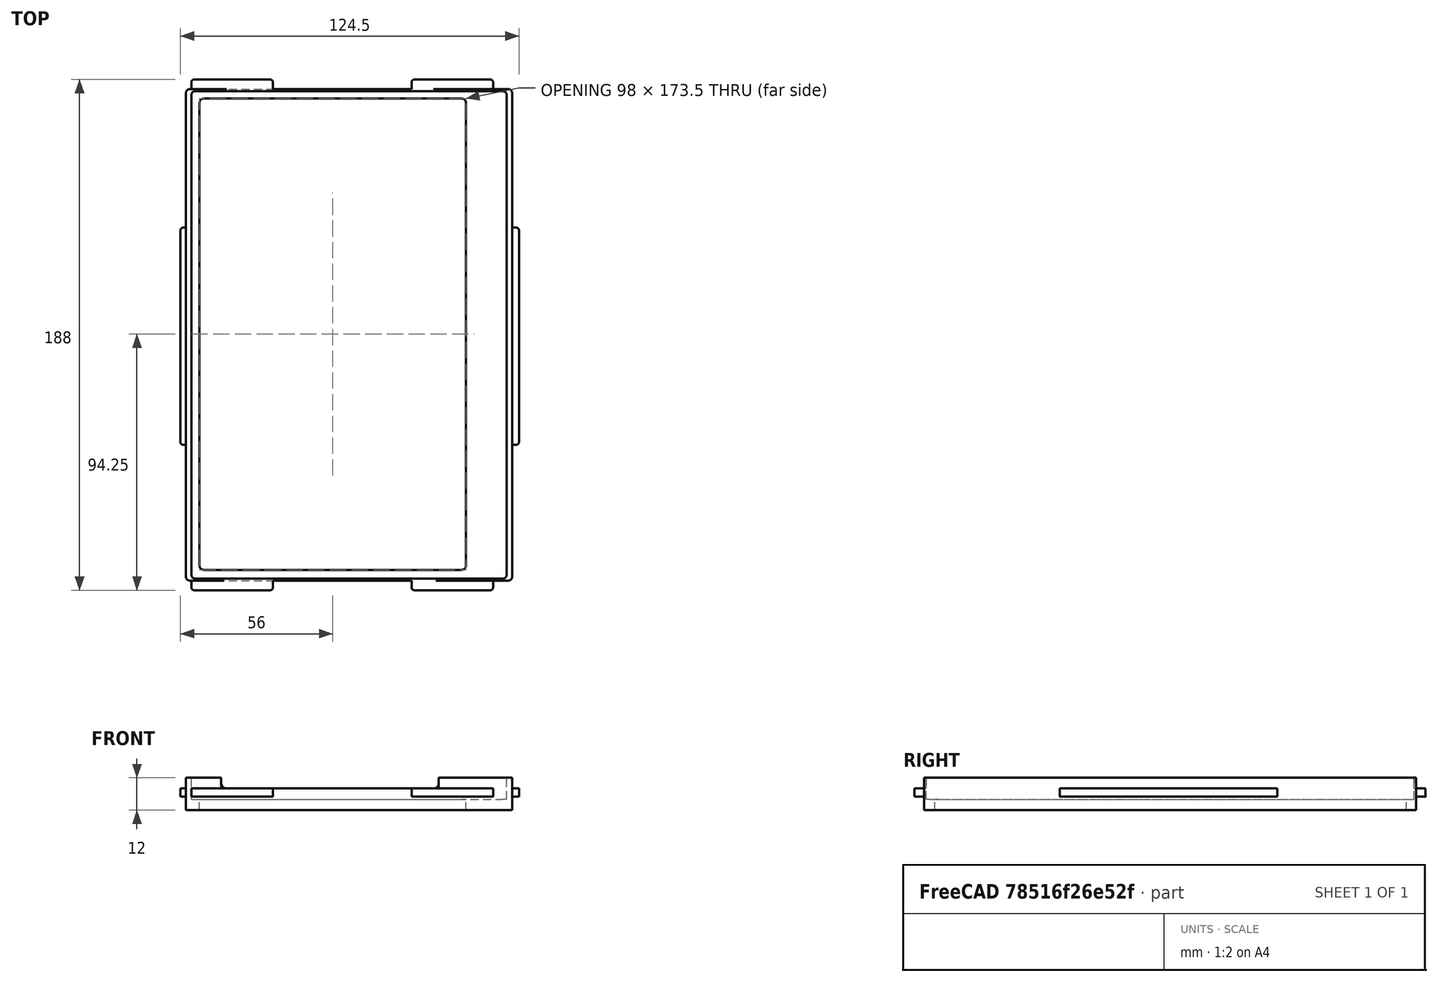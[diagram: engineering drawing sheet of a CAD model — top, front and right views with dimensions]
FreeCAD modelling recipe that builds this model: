
FCSTD DOCUMENT  (FreeCAD 0.20R29177 (Git))
Label: carrier-atoto-s8_test_g
License: All rights reserved
LicenseURL: http://en.wikipedia.org/wiki/All_rights_reserved
objects: Part::Box×12, Part::Fillet×11, Part::MultiFuse×4, Part::Cut×3
note: 30 computed .brp shape members not serialized (recipe doc carries the construction recipe); baked Part::Feature solids carry a one-line shape summary decoded from their .brp

FEATURE [Part::Box] Box  label="Cube"
  AttacherType = Attacher::AttachEngine3D
  Height = 4
  Length = 120
  Placement = pos=(2,0,0) rot=(0,0,1;0rad)
  Width = 181
FEATURE [Part::Box] Box001  label="Cube001"
  AttacherType = Attacher::AttachEngine3D
  Height = 4
  Length = 98
  Placement = pos=(7,4,0) rot=(0,0,1;0rad)
  Width = 173.5
FEATURE [Part::Fillet] Fillet
  Base = -> Box001
  Edges = 4 edges r=1.5: [Edge1,Edge3,Edge5,Edge7]
FEATURE [Part::Fillet] Fillet001
  Base = -> Box
  Edges = 4 edges r=1.5: [Edge1,Edge3,Edge5,Edge7]
FEATURE [Part::Cut] Cut
  Base = -> Fillet001
  Tool = -> Fillet
FEATURE [Part::Box] Box002  label="Cube002"
  AttacherType = Attacher::AttachEngine3D
  Height = 8
  Length = 120
  Placement = pos=(2,0,4) rot=(0,0,1;0rad)
  Width = 181
FEATURE [Part::Box] Box003  label="Cube003"
  AttacherType = Attacher::AttachEngine3D
  Height = 10
  Length = 116
  Placement = pos=(4,0.75,4) rot=(0,0,1;0rad)
  Width = 179.5
FEATURE [Part::Fillet] Fillet002
  Base = -> Box003
  Edges = 4 edges r=1.5: [Edge1,Edge3,Edge5,Edge7]
FEATURE [Part::Fillet] Fillet003
  Base = -> Box002
  Edges = 4 edges r=1.5: [Edge1,Edge3,Edge5,Edge7]
FEATURE [Part::Cut] Cut001
  Base = -> Fillet003
  Tool = -> Fillet002
FEATURE [Part::Box] Box006  label="Cube006"
  AttacherType = Attacher::AttachEngine3D
  Height = 10
  Length = 80
  Placement = pos=(15,-5,0) rot=(0,0,1;0rad)
  Width = 10
FEATURE [Part::Box] Box007  label="Cube007"
  AttacherType = Attacher::AttachEngine3D
  Height = 10
  Length = 80
  Placement = pos=(15,175,0) rot=(0,0,1;0rad)
  Width = 10
FEATURE [Part::MultiFuse] Fusion
  Placement = pos=(0,0,8) rot=(0,0,1;0rad)
  Shapes = -> [Box007,Box006]
FEATURE [Part::Fillet] Fillet004
  Base = -> Fusion
  Edges = 4 edges: [Edge4 r=2,Edge8 r=2,Edge16 r=1,Edge20 r=1]
FEATURE [Part::Cut] Cut002
  Base = -> Cut001
  Tool = -> Fillet004
FEATURE [Part::MultiFuse] Fusion001
  Shapes = -> [Cut,Cut002]
FEATURE [Part::Box] Box008  label="Cube008"
  AttacherType = Attacher::AttachEngine3D
  Height = 3
  Length = 30
  Placement = pos=(85,180.5,5) rot=(0,0,1;0rad)
  Width = 4
FEATURE [Part::Box] Box009  label="Cube009"
  AttacherType = Attacher::AttachEngine3D
  Height = 3
  Length = 30
  Placement = pos=(4,180.5,5) rot=(0,0,1;0rad)
  Width = 4
FEATURE [Part::Box] Box010  label="Cube010"
  AttacherType = Attacher::AttachEngine3D
  Height = 3
  Length = 30
  Placement = pos=(85,-3.5,5) rot=(0,0,1;0rad)
  Width = 4
FEATURE [Part::Box] Box011  label="Cube011"
  AttacherType = Attacher::AttachEngine3D
  Height = 3
  Length = 4
  Placement = pos=(0,50,5) rot=(0,0,1;0rad)
  Width = 80
FEATURE [Part::Box] Box012  label="Cube012"
  AttacherType = Attacher::AttachEngine3D
  Height = 3
  Length = 30
  Placement = pos=(4,-3.5,5) rot=(0,0,1;0rad)
  Width = 4
FEATURE [Part::Box] Box013  label="Cube013"
  AttacherType = Attacher::AttachEngine3D
  Height = 3
  Length = 4
  Placement = pos=(120.5,50,5) rot=(0,0,1;0rad)
  Width = 80
FEATURE [Part::Fillet] Fillet005
  Base = -> Box012
  Edges = 2 edges r=1: [Edge1,Edge5]
FEATURE [Part::Fillet] Fillet006
  Base = -> Box011
  Edges = 2 edges r=1: [Edge1,Edge3]
FEATURE [Part::Fillet] Fillet007
  Base = -> Box010
  Edges = 2 edges r=1: [Edge1,Edge5]
FEATURE [Part::Fillet] Fillet008
  Base = -> Box009
  Edges = 2 edges r=1: [Edge3,Edge7]
FEATURE [Part::Fillet] Fillet009
  Base = -> Box008
  Edges = 2 edges r=1: [Edge3,Edge7]
FEATURE [Part::Fillet] Fillet010
  Base = -> Box013
  Edges = 2 edges r=1: [Edge5,Edge7]
FEATURE [Part::MultiFuse] Fusion002
  Shapes = -> [Fillet005,Fillet006,Fillet007,Fillet008,Fillet009,Fillet010]
FEATURE [Part::MultiFuse] Fusion003
  Shapes = -> [Fusion001,Fusion002]
